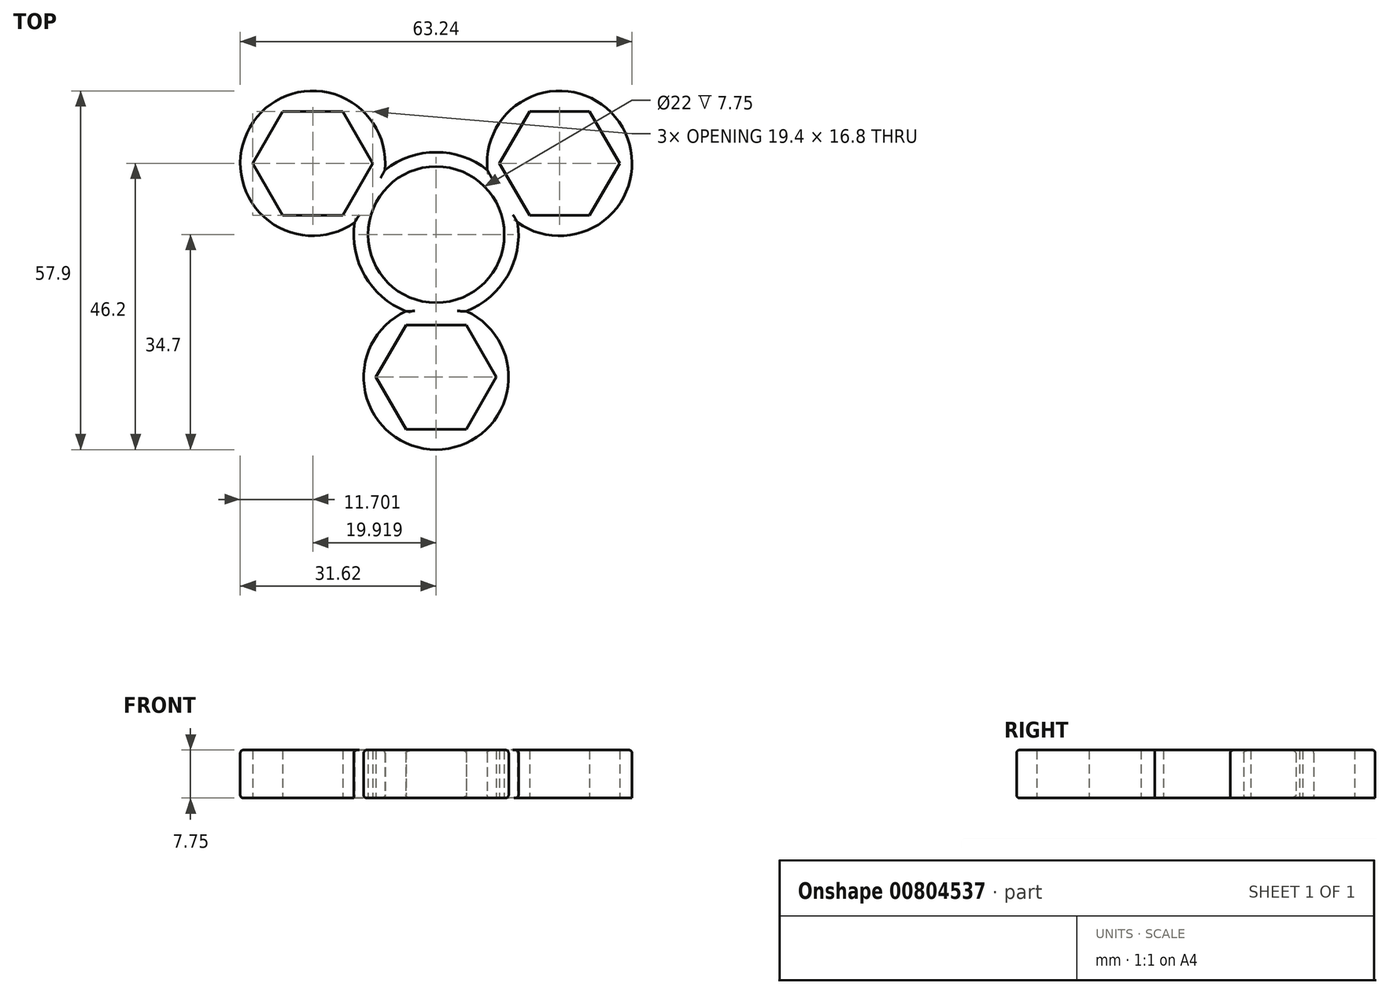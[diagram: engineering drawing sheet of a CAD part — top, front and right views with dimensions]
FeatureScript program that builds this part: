
annotation { "Feature Type Name" : "Feature", "Feature Type Description" : "" }
export const myFeature = defineFeature(function(context is Context, id is Id, definition is map)
    precondition{}
    {
        {
            var Q0;
            Q0=qCreatedBy(makeId("Top.planeOp"),FACE);
            var sketch = newSketch(context, id + "F0", { "sketchPlane" : qUnion([Q0])});
            skCircle(sketch, "E0", {"center": v(0, 0) * mm, "radius": 13.3 * mm});
            skCircle(sketch, "E1", {"center": v(0, -23) * mm, "radius": 11.7 * mm});
            skCircle(sketch, "E2", {"center": v(19.92, 11.5) * mm, "radius": 11.7 * mm});
            skCircle(sketch, "E3", {"center": v(-19.92, 11.5) * mm, "radius": 11.7 * mm});
            skLineSegment(sketch, "E4", {"start": v(-48.98, 58.94) * mm, "end": v(-57.64, 53.94) * mm, "construction": true});
            skLineSegment(sketch, "E5", {"start": v(-48.98, 58.94) * mm, "end": v(-48.98, 68.94) * mm, "construction": true});
            skLineSegment(sketch, "E6", {"start": v(-48.98, 58.94) * mm, "end": v(-40.32, 53.94) * mm, "construction": true});
            skCircle(sketch, "E7", {"center": v(-40.32, 53.94) * mm, "radius": 2.5 * mm});
            skCircle(sketch, "E8", {"center": v(-57.64, 53.94) * mm, "radius": 2.5 * mm});
            skCircle(sketch, "E9", {"center": v(-48.98, 68.94) * mm, "radius": 2.5 * mm});
            skCircle(sketch, "E10.cCircle", {"center": v(-48.98, 68.94) * mm, "radius": 1.68 * mm, "construction": true});
            skLineSegment(sketch, "E10.0", {"start": v(-47.05, 68.82) * mm, "end": v(-48.12, 67.2) * mm});
            skLineSegment(sketch, "E10.1", {"start": v(-48.12, 67.2) * mm, "end": v(-50.05, 67.33) * mm});
            skLineSegment(sketch, "E10.2", {"start": v(-50.05, 67.33) * mm, "end": v(-50.91, 69.06) * mm});
            skLineSegment(sketch, "E10.3", {"start": v(-50.91, 69.06) * mm, "end": v(-49.84, 70.68) * mm});
            skLineSegment(sketch, "E10.4", {"start": v(-49.84, 70.68) * mm, "end": v(-47.9, 70.55) * mm});
            skLineSegment(sketch, "E10.5", {"start": v(-47.9, 70.55) * mm, "end": v(-47.05, 68.82) * mm});
            skPoint(sketch, "E10.0.midPoint", {"position": v(-47.58, 68.01) * mm});
            skLineSegment(sketch, "E11", {"start": v(-19.92, 11.5) * mm, "end": v(0, 0) * mm, "construction": true});
            skLineSegment(sketch, "E12", {"start": v(19.92, 11.5) * mm, "end": v(0, 0) * mm, "construction": true});
            skLineSegment(sketch, "E13", {"start": v(0, -23) * mm, "end": v(0, 0) * mm, "construction": true});
            skCircle(sketch, "E14.cCircle", {"center": v(-19.92, 11.5) * mm, "radius": 8.4 * mm, "construction": true});
            skLineSegment(sketch, "E14.0", {"start": v(-24.77, 19.9) * mm, "end": v(-15.07, 19.9) * mm});
            skLineSegment(sketch, "E14.1", {"start": v(-15.07, 19.9) * mm, "end": v(-10.22, 11.5) * mm});
            skLineSegment(sketch, "E14.2", {"start": v(-10.22, 11.5) * mm, "end": v(-15.07, 3.1) * mm});
            skLineSegment(sketch, "E14.3", {"start": v(-15.07, 3.1) * mm, "end": v(-24.77, 3.1) * mm});
            skLineSegment(sketch, "E14.4", {"start": v(-24.77, 3.1) * mm, "end": v(-29.62, 11.5) * mm});
            skLineSegment(sketch, "E14.5", {"start": v(-29.62, 11.5) * mm, "end": v(-24.77, 19.9) * mm});
            skPoint(sketch, "E14.0.midPoint", {"position": v(-19.92, 19.9) * mm});
            skLineSegment(sketch, "E15.1.0", {"start": v(4.85, -31.4) * mm, "end": v(-4.85, -31.4) * mm});
            skLineSegment(sketch, "E15.1.1", {"start": v(-4.85, -31.4) * mm, "end": v(-9.7, -23) * mm});
            skLineSegment(sketch, "E15.1.2", {"start": v(-9.7, -23) * mm, "end": v(-4.85, -14.6) * mm});
            skLineSegment(sketch, "E15.1.3", {"start": v(-4.85, -14.6) * mm, "end": v(4.85, -14.6) * mm});
            skLineSegment(sketch, "E15.1.4", {"start": v(4.85, -14.6) * mm, "end": v(9.7, -23) * mm});
            skLineSegment(sketch, "E15.1.5", {"start": v(9.7, -23) * mm, "end": v(4.85, -31.4) * mm});
            skLineSegment(sketch, "E15.2.0", {"start": v(24.77, 19.9) * mm, "end": v(29.62, 11.5) * mm});
            skLineSegment(sketch, "E15.2.1", {"start": v(29.62, 11.5) * mm, "end": v(24.77, 3.1) * mm});
            skLineSegment(sketch, "E15.2.2", {"start": v(24.77, 3.1) * mm, "end": v(15.07, 3.1) * mm});
            skLineSegment(sketch, "E15.2.3", {"start": v(15.07, 3.1) * mm, "end": v(10.22, 11.5) * mm});
            skLineSegment(sketch, "E15.2.4", {"start": v(10.22, 11.5) * mm, "end": v(15.07, 19.9) * mm});
            skLineSegment(sketch, "E15.2.5", {"start": v(15.07, 19.9) * mm, "end": v(24.77, 19.9) * mm});
            skCircle(sketch, "E16", {"center": v(0, 0) * mm, "radius": 11 * mm});
            skSolve(sketch);
        }
        {
            var Q0;
            Q0=makeQuery(id+"F0.imprint","IMPRINT",FACE,{"disambiguationData":[TD([[makeQuery(id+"F0.imprint","IMPRINT",EDGE,{"derivedFrom":sQuery(id+"F0.wireOp",EDGE,"E14.0")}),1.0]])]});
            var Q1;
            Q1=makeQuery(id+"F0.imprint","IMPRINT",FACE,{"disambiguationData":[TD([[makeQuery(id+"F0.imprint","IMPRINT",EDGE,{"derivedFrom":sQuery(id+"F0.wireOp",EDGE,"E15.2.0")}),1.0]])]});
            var Q2;
            Q2=makeQuery(id+"F0.imprint","IMPRINT",FACE,{"disambiguationData":[TD([[makeQuery(id+"F0.imprint","IMPRINT",EDGE,{"derivedFrom":sQuery(id+"F0.wireOp",EDGE,"E15.1.0")}),1.0]])]});
            var Q3;
            {var subQ0=sQuery(id+"F0.wireOp",EDGE,"E3");var subQ1=sQuery(id+"F0.wireOp",EDGE,"E0");var subQ2=makeQuery(id+"F0.imprint","INTERSECT",VERTEX,{"disambiguationData":[OD(0.0)],"derivedFrom":[subQ1,subQ0]});Q3=makeQuery(id+"F0.imprint","IMPRINT",FACE,{"disambiguationData":[TD([[makeQuery(id+"F0.imprint","IMPRINT",EDGE,{"disambiguationData":[TD([[subQ2,-1.0]])],"derivedFrom":subQ1}),1.0]])]});}
            var Q4;
            {var subQ0=sQuery(id+"F0.wireOp",EDGE,"E1");var subQ1=sQuery(id+"F0.wireOp",EDGE,"E0");var subQ2=makeQuery(id+"F0.imprint","INTERSECT",VERTEX,{"disambiguationData":[OD(0.0)],"derivedFrom":[subQ1,subQ0]});Q4=makeQuery(id+"F0.imprint","IMPRINT",FACE,{"disambiguationData":[TD([[makeQuery(id+"F0.imprint","IMPRINT",EDGE,{"disambiguationData":[TD([[subQ2,-1.0]])],"derivedFrom":subQ1}),1.0]])]});}
            var Q5;
            Q5=makeQuery(id+"F0.imprint","IMPRINT",FACE,{"disambiguationData":[TD([[makeQuery(id+"F0.imprint","IMPRINT",EDGE,{"derivedFrom":sQuery(id+"F0.wireOp",EDGE,"E16")}),-1.0]])]});
            var Q6;
            {var subQ0=sQuery(id+"F0.wireOp",EDGE,"E2");var subQ1=sQuery(id+"F0.wireOp",EDGE,"E0");var subQ2=makeQuery(id+"F0.imprint","INTERSECT",VERTEX,{"disambiguationData":[OD(0.0)],"derivedFrom":[subQ1,subQ0]});Q6=makeQuery(id+"F0.imprint","IMPRINT",FACE,{"disambiguationData":[TD([[makeQuery(id+"F0.imprint","IMPRINT",EDGE,{"disambiguationData":[TD([[subQ2,1.0]])],"derivedFrom":subQ1}),1.0]])]});}
            extrude(context, id + "F1", {"entities" : qUnion([Q0, Q1, Q2, Q3, Q4, Q5, Q6]), "depth" : 7.75 * mm, "offsetDistance" : 25 * mm});
        }
        {
            var Q0;
            Q0=makeQuery(id+"F1.opExtrude","CAP_EDGE",EDGE,{"disambiguationData":[OSD([sQuery(id+"F0.wireOp",EDGE,"E1")])],"isStart":false});
            var Q1;
            Q1=makeQuery(id+"F1.opExtrude","CAP_EDGE",EDGE,{"disambiguationData":[OSD([sQuery(id+"F0.wireOp",EDGE,"E2")])],"isStart":false});
            var Q2;
            {var subQ0=sQuery(id+"F0.wireOp",EDGE,"E0");Q2=makeQuery(id+"F1.opExtrude","CAP_EDGE",EDGE,{"disambiguationData":[OSD([subQ0]),TDD([makeQuery(id+"F0.imprint","IMPRINT",EDGE,{"disambiguationData":[TD([[makeQuery(id+"F0.imprint","INTERSECT",VERTEX,{"disambiguationData":[OD(1.0)],"derivedFrom":[subQ0,sQuery(id+"F0.wireOp",EDGE,"E2")]}),1.0]])],"derivedFrom":subQ0})])],"isStart":false});}
            var Q3;
            {var subQ0=sQuery(id+"F0.wireOp",EDGE,"E0");Q3=makeQuery(id+"F1.opExtrude","CAP_EDGE",EDGE,{"disambiguationData":[OSD([subQ0]),TDD([makeQuery(id+"F0.imprint","IMPRINT",EDGE,{"disambiguationData":[TD([[makeQuery(id+"F0.imprint","INTERSECT",VERTEX,{"disambiguationData":[OD(0.0)],"derivedFrom":[subQ0,sQuery(id+"F0.wireOp",EDGE,"E2")]}),-1.0]])],"derivedFrom":subQ0})])],"isStart":false});}
            var Q4;
            Q4=makeQuery(id+"F1.opExtrude","CAP_EDGE",EDGE,{"disambiguationData":[OSD([sQuery(id+"F0.wireOp",EDGE,"E3")])],"isStart":false});
            var Q5;
            {var subQ0=sQuery(id+"F0.wireOp",EDGE,"E0");Q5=makeQuery(id+"F1.opExtrude","CAP_EDGE",EDGE,{"disambiguationData":[OSD([subQ0]),TDD([makeQuery(id+"F0.imprint","IMPRINT",EDGE,{"disambiguationData":[TD([[makeQuery(id+"F0.imprint","INTERSECT",VERTEX,{"disambiguationData":[OD(1.0)],"derivedFrom":[subQ0,sQuery(id+"F0.wireOp",EDGE,"E3")]}),-1.0]])],"derivedFrom":subQ0})])],"isStart":false});}
            var Q6;
            Q6=makeQuery(id+"F1.opExtrude","CAP_EDGE",EDGE,{"disambiguationData":[OSD([sQuery(id+"F0.wireOp",EDGE,"E1")])],"isStart":true});
            var Q7;
            {var subQ0=sQuery(id+"F0.wireOp",EDGE,"E0");Q7=makeQuery(id+"F1.opExtrude","CAP_EDGE",EDGE,{"disambiguationData":[OSD([subQ0]),TDD([makeQuery(id+"F0.imprint","IMPRINT",EDGE,{"disambiguationData":[TD([[makeQuery(id+"F0.imprint","INTERSECT",VERTEX,{"disambiguationData":[OD(1.0)],"derivedFrom":[subQ0,sQuery(id+"F0.wireOp",EDGE,"E2")]}),1.0]])],"derivedFrom":subQ0})])],"isStart":true});}
            var Q8;
            {var subQ0=sQuery(id+"F0.wireOp",EDGE,"E0");Q8=makeQuery(id+"F1.opExtrude","CAP_EDGE",EDGE,{"disambiguationData":[OSD([subQ0]),TDD([makeQuery(id+"F0.imprint","IMPRINT",EDGE,{"disambiguationData":[TD([[makeQuery(id+"F0.imprint","INTERSECT",VERTEX,{"disambiguationData":[OD(0.0)],"derivedFrom":[subQ0,sQuery(id+"F0.wireOp",EDGE,"E2")]}),-1.0]])],"derivedFrom":subQ0})])],"isStart":true});}
            var Q9;
            Q9=makeQuery(id+"F1.opExtrude","CAP_EDGE",EDGE,{"disambiguationData":[OSD([sQuery(id+"F0.wireOp",EDGE,"E3")])],"isStart":true});
            fillet(context, id + "F2", {"entities" : qUnion([Q0, Q1, Q2, Q3, Q4, Q5, Q6, Q7, Q8, Q9]), "radius" : 0.5 * mm, "tangentPropagation" : true, "allowEdgeOverflow" : false});
        }
    });
